# Revit family: Flat roof window FAKRO DXF DU8
name_source: partatom
category: Okna
revit_build: Autodesk Revit 2015 (Build: 20140606_1530(x64)
units: mm (PartAtom-declared; Revit-internal decimal feet)

## types (1)
- Flat roof window FAKRO DXF DU8
    Apron Material = Fakro - aluminium RAL7022
    Bimobject Category = Windows - Roof Windows
    CSI MasterFormat 2016 Code = 08 60 00
    CSI MasterFormat 2016 Title = Roof Windows and Skylights
    CSI UniFormat II Code = B3020
    CSI UniFormat II Title = Roof Openings
    Glazing = Fakro - Glass
    IFC Classification = Window
    Kod zespołu = B3020110
    Material External = Fakro - aluminium RAL7022
    Material Internal = Fakro - frame PVC RAL 9010
    Model = DXF DU8
    NBS Reference = 59-72
    NBS Reference Description = Roof Windows Units
    Obj Type = 1 mm  [stored 0.00328084 ft]
    Opis = Flat roof window
    Producent = FAKRO
    Szerokość = 600 mm  [stored 1.9685 ft]
    UNSPC Category = Skylights
    UNSPC Code = 301718
    URL = www.fakro.com
    Uniclass 1.4 Code = JL1
    Uniclass 1.4 Description = Windows/Rooflights/Screens/Louvres
    Uniclass 2.0 Code = PR-59-72
    Uniclass 2.0 Description = Roof Windows Units
    Uniclass 2015 Code = PR_30_59_72_77
    Uniclass 2015 Title = Skylights
    Wysokość = 190 mm
    air permeability class EN 14351-1:2006+A1:2010 = 4
    frame thermal insulation Uf [W/m2K] EN 14351-1:2006+A1:2010 = 0.69
    glass structure = 6H-10-4HT-10-4HT-12-44.2T
    glazing U-value [W/m2K] EN 14351-1:2006+A1:2010 = 0.4
    glazing area = 0.23 m²
    impact resistance class EN 14351-1:2006+A1:2010 = 5
    light transmittance factor tv EN 14351-1:2006+A1:2010 = 0.49
    material = frame PVC
    opening method = non-opening
    reaction to fire EN 14351-1:2006+A1:2010 = B-s2, d0
    resistance to snow load EN 14351-1:2006+A1:2010 = 6H-10-4H-10-4H-12-44.2
    resistance to wind load EN 14351-1:2006+A1:2010 = C5/B5
    roof angle = 2 -15
    solar factor [ g] EN 14351-1:2006+A1:2010 = 0.3
    watertightness / unshielded (A) EN 14351-1:2006+A1:2010 = E1200
    window acoustic performance Rw [dB] EN 14351-1:2006+A1:2010 = 33(-1;-3)
    window area by the dimensions of the base = 0.67 m²
    window heat transfer coefficient Uw [W/m2K] EN 14351-1:2006+A1:2010 = 0.64
    window internal area = 0.25 m²
    window perimeter = 3280 mm  [stored 10.7612 ft]
    window weight = 43.00 kg

note: [stored X ft] marks values corroborated as IEEE doubles in the binary element streams (Revit-internal decimal feet)
